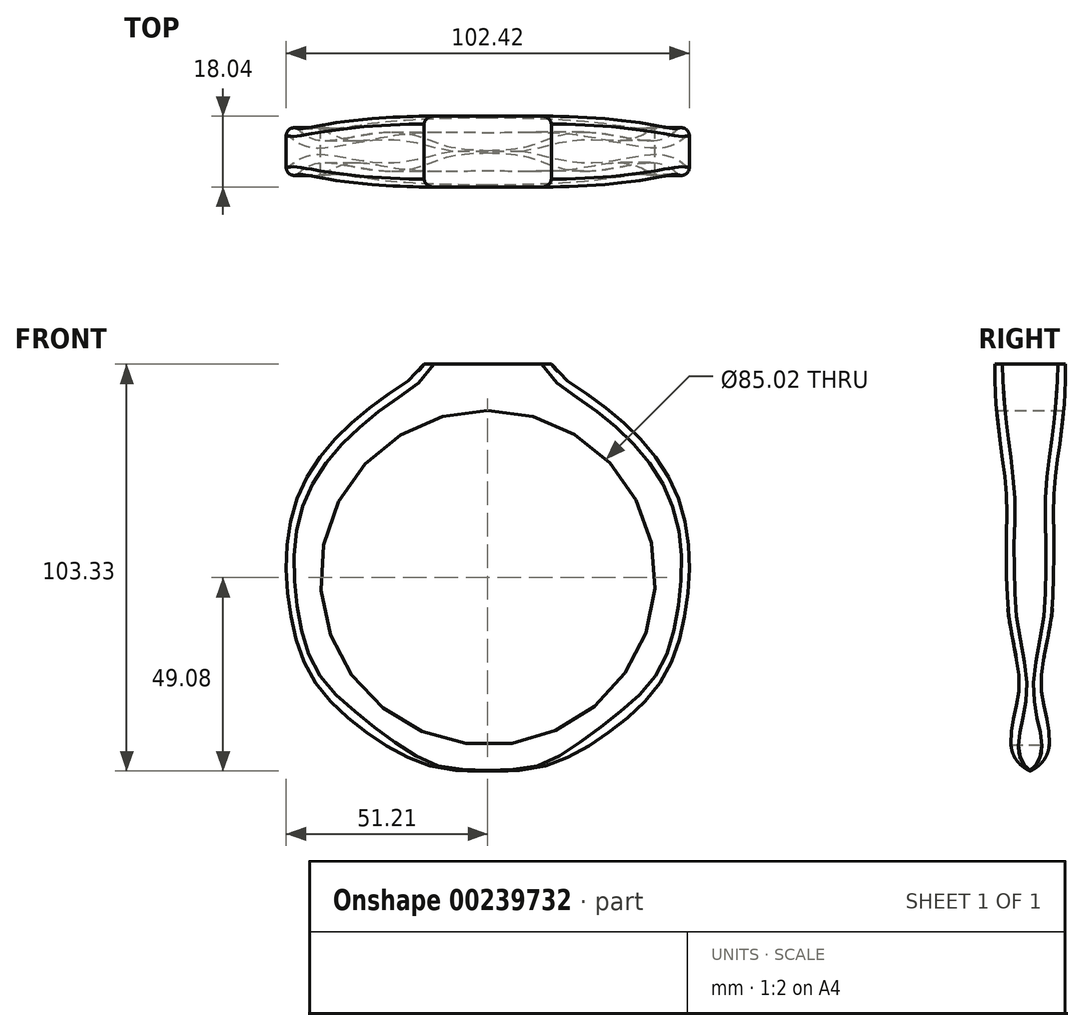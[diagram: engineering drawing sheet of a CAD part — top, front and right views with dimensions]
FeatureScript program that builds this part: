
annotation { "Feature Type Name" : "Feature", "Feature Type Description" : "" }
export const myFeature = defineFeature(function(context is Context, id is Id, definition is map)
    precondition{}
    {
        {
            var Q0;
            Q0=qCreatedBy(makeId("Front.planeOp"),FACE);
            var sketch = newSketch(context, id + "F0", { "sketchPlane" : qUnion([Q0])});
            skCircle(sketch, "E0", {"center": v(0, 0) * mm, "radius": 42.5 * mm});
            skFitSpline(sketch, "E1", {"points": [v(-16.14, 54.25) * mm, v(-24.4, 47.17) * mm, v(-39.24, 34.71) * mm, v(-50.46, 12.51) * mm, v(-47.06, -20.44) * mm, v(-35.21, -35.81) * mm, v(-17.04, -47.06) * mm, v(0, -49.17) * mm], "startDerivative": vector(-91.72, -120.4) * mm, "endDerivative": vector(152.25, -1.76) * mm});
            skFitSpline(sketch, "E2.MirrorCS", {"points": [v(16.14, 54.25) * mm, v(24.4, 47.17) * mm, v(39.24, 34.71) * mm, v(50.46, 12.51) * mm, v(47.06, -20.44) * mm, v(35.21, -35.81) * mm, v(17.04, -47.06) * mm, v(0, -49.17) * mm], "startDerivative": vector(91.72, -120.4) * mm, "endDerivative": vector(-152.25, -1.76) * mm});
            skLineSegment(sketch, "E3", {"start": v(-16.14, 54.25) * mm, "end": v(16.14, 54.25) * mm});
            skSolve(sketch);
        }
        {
            var Q0;
            Q0=qCreatedBy(makeId("Right.planeOp"),FACE);
            var sketch = newSketch(context, id + "F1", { "sketchPlane" : qUnion([Q0])});
            skFitSpline(sketch, "E4.0", {"points": [v(0, 54.25) * mm, v(0, 50.06) * mm, v(0, 47.92) * mm, v(0, 34.9) * mm, v(0, 13.57) * mm, v(0, -21.76) * mm, v(0, -35.97) * mm, v(0, -48.95) * mm, v(0, -49.1) * mm, v(0, -49.17) * mm]});
            skLineSegment(sketch, "E4.1", {"start": v(0, -42.5) * mm, "end": v(0, 42.5) * mm});
            skFitSpline(sketch, "E4.2", {"points": [v(0, 54.25) * mm, v(0, 50.06) * mm, v(0, 47.92) * mm, v(0, 34.9) * mm, v(0, 13.57) * mm, v(0, -21.76) * mm, v(0, -35.97) * mm, v(0, -48.95) * mm, v(0, -49.1) * mm, v(0, -49.17) * mm]});
            skFitSpline(sketch, "E5", {"points": [v(-9, 54.25) * mm, v(-6.65, 27.51) * mm, v(-5.86, 16.19) * mm, v(-6.08, 7.24) * mm, v(-5.86, -3.3) * mm, v(-5.52, -9.4) * mm, v(-3.25, -21.87) * mm, v(-3.48, -32.51) * mm, v(0.15, -49.17) * mm], "startDerivative": vector(-2.82, -170.23) * mm, "endDerivative": vector(155, -68.48) * mm});
            skSolve(sketch);
        }
        {
            var Q0;
            Q0=sQuery(id+"F1.wireOp",EDGE,"E5");
            extrude(context, id + "F2", {"bodyType" : ToolBodyType.SURFACE, "surfaceEntities" : qUnion([Q0]), "endBound" : BoundingType.SYMMETRIC, "depth" : 126.4 * mm});
        }
        {
            var Q0;
            Q0=makeQuery(id+"F0.imprint","IMPRINT",FACE,{"disambiguationData":[TD([[makeQuery(id+"F0.imprint","IMPRINT",EDGE,{"derivedFrom":sQuery(id+"F0.wireOp",EDGE,"E0")}),-1.0]])]});
            extrude(context, id + "F3", {"entities" : qUnion([Q0]), "endBound" : BoundingType.UP_TO_NEXT, "depth" : 25 * mm});
        }
        {
            var Q0;
            Q0=makeQuery(id+"F3.opExtrude","CAP_EDGE",EDGE,{"disambiguationData":[OSD([sQuery(id+"F0.wireOp",EDGE,"E1")])],"isStart":false});
            var Q1;
            Q1=makeQuery(id+"F3.opExtrude","CAP_EDGE",EDGE,{"disambiguationData":[OSD([sQuery(id+"F0.wireOp",EDGE,"E2.MirrorCS")])],"isStart":false});
            fillet(context, id + "F4", {"entities" : qUnion([Q0, Q1]), "radius" : 2 * mm, "tangentPropagation" : true, "allowEdgeOverflow" : false});
        }
        {
            var Q0;
            Q0=makeQuery(id+"F3.opExtrude","SWEPT_BODY",BODY,{"disambiguationData":[OSD([sQuery(id+"F0.wireOp",EDGE,"E0"),sQuery(id+"F0.wireOp",EDGE,"E1"),sQuery(id+"F0.wireOp",EDGE,"E2.MirrorCS"),sQuery(id+"F0.wireOp",EDGE,"E3")])]});
            var Q1;
            Q1=qCreatedBy(makeId("Front.planeOp"),FACE);
            mirror(context, id + "F5", {"operationType" : NewBodyOperationType.ADD, "entities" : qUnion([Q0]), "mirrorPlane" : qUnion([Q1])});
        }
    });
